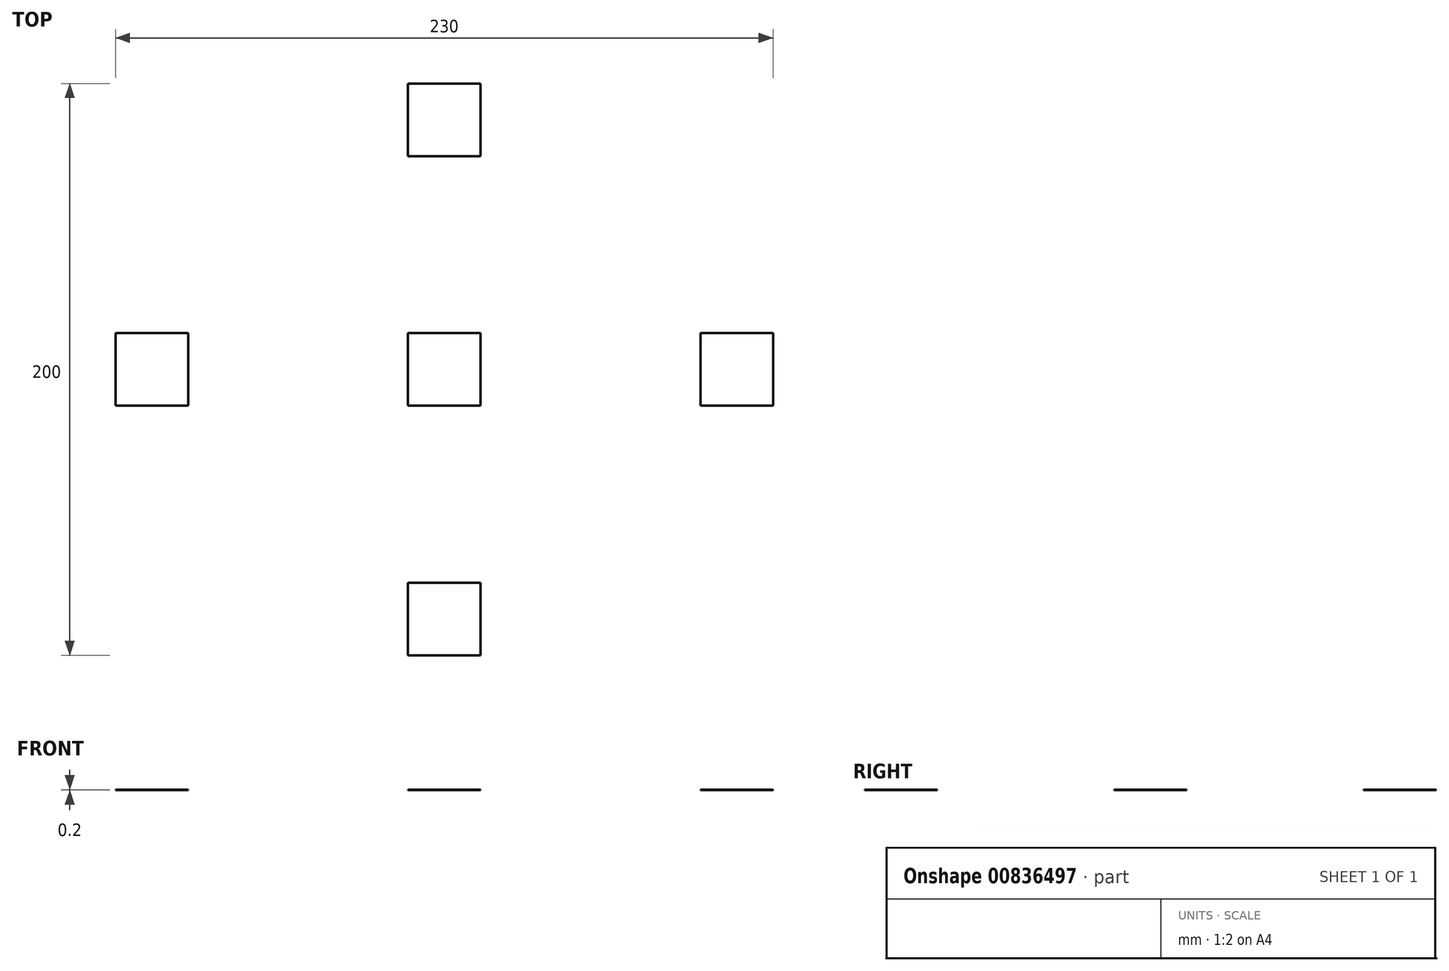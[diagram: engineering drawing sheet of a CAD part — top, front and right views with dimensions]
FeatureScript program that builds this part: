
annotation { "Feature Type Name" : "Feature", "Feature Type Description" : "" }
export const myFeature = defineFeature(function(context is Context, id is Id, definition is map)
    precondition{}
    {
        {
            var Q0;
            Q0=qCreatedBy(makeId("Top.planeOp"),FACE);
            var sketch = newSketch(context, id + "F0", { "sketchPlane" : qUnion([Q0])});
            skLineSegment(sketch, "E0.bottom", {"start": v(12.7, -12.7) * mm, "end": v(-12.7, -12.7) * mm});
            skLineSegment(sketch, "E0.top", {"start": v(12.7, 12.7) * mm, "end": v(-12.7, 12.7) * mm});
            skLineSegment(sketch, "E0.left", {"start": v(12.7, -12.7) * mm, "end": v(12.7, 12.7) * mm});
            skLineSegment(sketch, "E0.right", {"start": v(-12.7, -12.7) * mm, "end": v(-12.7, 12.7) * mm});
            skPoint(sketch, "E0.middle", {"position": v(0, 0) * mm});
            skLineSegment(sketch, "E1.bottom", {"start": v(115, -12.7) * mm, "end": v(89.6, -12.7) * mm});
            skLineSegment(sketch, "E1.top", {"start": v(115, 12.7) * mm, "end": v(89.6, 12.7) * mm});
            skLineSegment(sketch, "E1.left", {"start": v(115, -12.7) * mm, "end": v(115, 12.7) * mm});
            skLineSegment(sketch, "E1.right", {"start": v(89.6, -12.7) * mm, "end": v(89.6, 12.7) * mm});
            skPoint(sketch, "E1.middle", {"position": v(102.3, 0) * mm});
            skLineSegment(sketch, "E2.bottom", {"start": v(-89.6, -12.7) * mm, "end": v(-115, -12.7) * mm});
            skLineSegment(sketch, "E2.top", {"start": v(-89.6, 12.7) * mm, "end": v(-115, 12.7) * mm});
            skLineSegment(sketch, "E2.left", {"start": v(-89.6, -12.7) * mm, "end": v(-89.6, 12.7) * mm});
            skLineSegment(sketch, "E2.right", {"start": v(-115, -12.7) * mm, "end": v(-115, 12.7) * mm});
            skPoint(sketch, "E2.middle", {"position": v(-102.3, 0) * mm});
            skLineSegment(sketch, "E3.bottom", {"start": v(12.7, 74.6) * mm, "end": v(-12.7, 74.6) * mm});
            skLineSegment(sketch, "E3.top", {"start": v(12.7, 100) * mm, "end": v(-12.7, 100) * mm});
            skLineSegment(sketch, "E3.left", {"start": v(12.7, 74.6) * mm, "end": v(12.7, 100) * mm});
            skLineSegment(sketch, "E3.right", {"start": v(-12.7, 74.6) * mm, "end": v(-12.7, 100) * mm});
            skPoint(sketch, "E3.middle", {"position": v(0, 87.3) * mm});
            skLineSegment(sketch, "E4.bottom", {"start": v(12.7, -100) * mm, "end": v(-12.7, -100) * mm});
            skLineSegment(sketch, "E4.top", {"start": v(12.7, -74.6) * mm, "end": v(-12.7, -74.6) * mm});
            skLineSegment(sketch, "E4.left", {"start": v(12.7, -100) * mm, "end": v(12.7, -74.6) * mm});
            skLineSegment(sketch, "E4.right", {"start": v(-12.7, -100) * mm, "end": v(-12.7, -74.6) * mm});
            skPoint(sketch, "E4.middle", {"position": v(0, -87.3) * mm});
            skSolve(sketch);
        }
        {
            var Q0;
            Q0=qSketchRegion(id+"F0",true);
            extrude(context, id + "F1", {"entities" : qUnion([Q0]), "depth" : .2 * mm, "offsetDistance" : 25.4 * mm});
        }
    });
